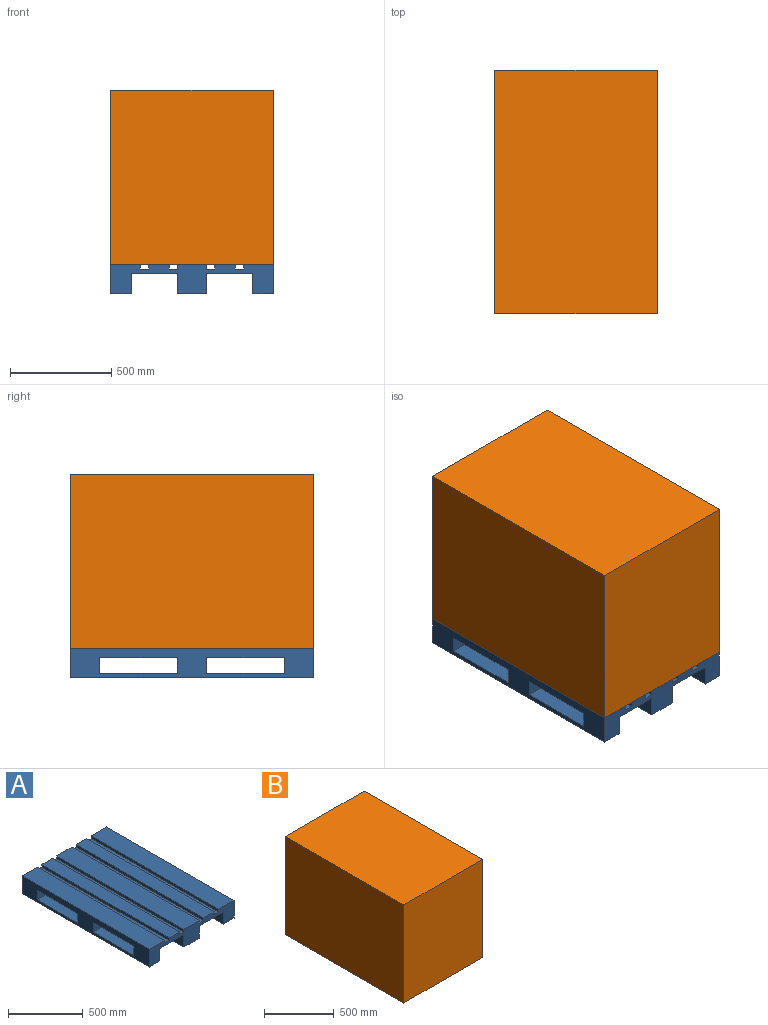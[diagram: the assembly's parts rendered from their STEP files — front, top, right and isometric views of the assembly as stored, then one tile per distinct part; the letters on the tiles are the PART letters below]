
ASSEMBLY  parts=2 mates=1
PART A: 47 faces, bbox 800x1200x144 mm
  f0: plane 1200x42.5mm, normal (0,0,1), area 51000mm2, adj f4,f6,f42,f45
  f1: plane 1200x40mm, normal (0,0,1), area 48000mm2, adj f4,f6,f40,f43
  f2: plane 1200x40mm, normal (0,0,1), area 48000mm2, adj f4,f6,f37,f39
  f3: plane 1200x800mm, normal (0,0,-1), area 809925mm2, adj f4,f5,f6,f7,f9,f10,f11,f12
  f4: plane 800x144mm, normal (0,1,0), area 66070mm2, adj f0,f1,f2,f3,f5,f7,f8,f9
  f5: plane 1200x144mm, normal (-1,0,0), area 113130mm2, adj f3,f4,f6,f10,f11,f12,f13,f25
  f6: plane 800x144mm, normal (0,-1,0), area 66070mm2, adj f0,f1,f2,f3,f5,f7,f8,f9
  f7: plane 1200x144mm, normal (1,0,0), area 113130mm2, adj f3,f4,f6,f20,f22,f23,f24,f31
  f8: plane 1200x42.5mm, normal (0,0,1), area 51000mm2, adj f4,f6,f34,f36
  f9: plane 1200x100mm, normal (1,0,0), area 60330mm2, adj f3,f4,f6,f10,f11,f12,f13,f25
  f10: plane 100x78mm, normal (0,1,0), area 7800mm2, adj f3,f5,f9,f25
  f11: plane 100x78mm, normal (0,-1,0), area 7800mm2, adj f3,f5,f9,f26
  f12: plane 100x78mm, normal (0,-1,0), area 7800mm2, adj f3,f5,f9,f25
  f13: plane 100x78mm, normal (0,1,0), area 7800mm2, adj f3,f5,f9,f26
  f14: plane 1200x100mm, normal (-1,0,0), area 60330mm2, adj f3,f4,f6,f15,f17,f18,f19,f28
  f15: plane 145x78mm, normal (0,1,0), area 11310mm2, adj f3,f14,f16,f29
  f16: plane 1200x100mm, normal (1,0,0), area 60330mm2, adj f3,f4,f6,f15,f17,f18,f19,f28
  f17: plane 145x78mm, normal (0,-1,0), area 11310mm2, adj f3,f14,f16,f28
  f18: plane 145x78mm, normal (0,-1,0), area 11310mm2, adj f3,f14,f16,f29
  f19: plane 145x78mm, normal (0,1,0), area 11310mm2, adj f3,f14,f16,f28
  f20: plane 100x78mm, normal (0,-1,0), area 7800mm2, adj f3,f7,f21,f32
  f21: plane 1200x100mm, normal (-1,0,0), area 60330mm2, adj f3,f4,f6,f20,f22,f23,f24,f31
  f22: plane 100x78mm, normal (0,1,0), area 7800mm2, adj f3,f7,f21,f31
  f23: plane 100x78mm, normal (0,1,0), area 7800mm2, adj f3,f7,f21,f32
  f24: plane 100x78mm, normal (0,-1,0), area 7800mm2, adj f3,f7,f21,f31
  f25: plane 382.5x100mm, normal (0,0,1), area 38250mm2, adj f5,f9,f10,f12
  f26: plane 382.5x100mm, normal (0,0,1), area 38250mm2, adj f5,f9,f11,f13
  f27: plane 1200x100mm, normal (0,0,-1), area 120000mm2, adj f4,f5,f6,f9
  f28: plane 382.5x145mm, normal (0,0,1), area 55462.5mm2, adj f14,f16,f17,f19
  f29: plane 382.5x145mm, normal (0,0,1), area 55462.5mm2, adj f14,f15,f16,f18
  f30: plane 1200x145mm, normal (0,0,-1), area 174000mm2, adj f4,f6,f14,f16
  f31: plane 382.5x100mm, normal (0,0,1), area 38250mm2, adj f7,f21,f22,f24
  f32: plane 382.5x100mm, normal (0,0,1), area 38250mm2, adj f7,f20,f21,f23
  f33: plane 1200x100mm, normal (0,0,-1), area 120000mm2, adj f4,f6,f7,f21
  f34: plane 1200x22mm, normal (1,0,0), area 26400mm2, adj f4,f6,f8,f35
  f35: plane 1200x145mm, normal (0,0,1), area 174000mm2, adj f4,f5,f6,f34
  f36: plane 1200x22mm, normal (-1,0,0), area 26400mm2, adj f4,f6,f8,f38
  f37: plane 1200x22mm, normal (1,0,0), area 26400mm2, adj f2,f4,f6,f38
  f38: plane 1200x100mm, normal (0,0,1), area 120000mm2, adj f4,f6,f36,f37
  f39: plane 1200x22mm, normal (-1,0,0), area 26400mm2, adj f2,f4,f6,f41
  f40: plane 1200x22mm, normal (1,0,0), area 26400mm2, adj f1,f4,f6,f41
  f41: plane 1200x145mm, normal (0,0,1), area 174000mm2, adj f4,f6,f39,f40
  f42: plane 1200x22mm, normal (1,0,0), area 26400mm2, adj f0,f4,f6,f44
  f43: plane 1200x22mm, normal (-1,0,0), area 26400mm2, adj f1,f4,f6,f44
  f44: plane 1200x100mm, normal (0,0,1), area 120000mm2, adj f4,f6,f42,f43
  f45: plane 1200x22mm, normal (-1,0,0), area 26400mm2, adj f0,f4,f6,f46
  f46: plane 1200x145mm, normal (0,0,1), area 174000mm2, adj f4,f6,f7,f45
PART B: 6 faces, bbox 800x1200x860 mm
  f0: plane 1200x860mm, normal (1,0,0), area 1032000mm2, adj f1,f3,f4,f5
  f1: plane 860x800mm, normal (0,1,0), area 688000mm2, adj f0,f2,f4,f5
  f2: plane 1200x860mm, normal (-1,0,0), area 1032000mm2, adj f1,f3,f4,f5
  f3: plane 860x800mm, normal (0,-1,0), area 688000mm2, adj f0,f2,f4,f5
  f4: plane 1200x800mm, normal (0,0,1), area 960000mm2, adj f0,f1,f2,f3
  f5: plane 1200x800mm, normal (0,0,-1), area 960000mm2, adj f0,f1,f2,f3
PLACE A t=(352.93,-226.22,-292.34)mm fixed
PLACE B t=(689.71,-826.22,-270.34)mm
MATE fastened B.f5 <-> A.f35  axis (0,0,-1) through (289.71,-1426.22,-270.34)mm
